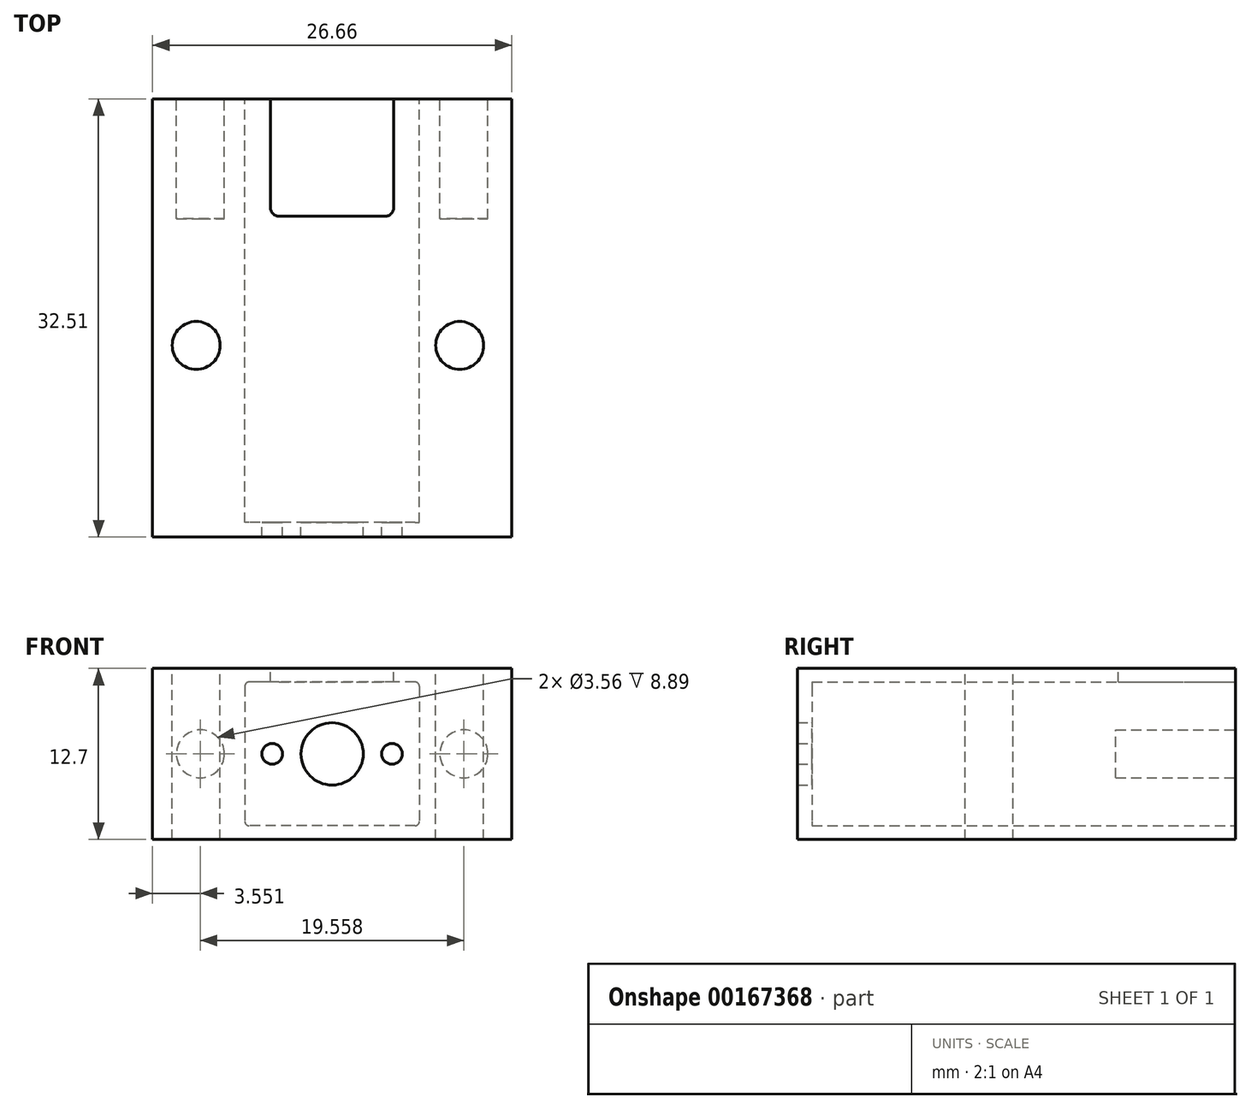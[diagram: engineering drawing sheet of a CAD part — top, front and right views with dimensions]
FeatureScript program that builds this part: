
annotation { "Feature Type Name" : "Feature", "Feature Type Description" : "" }
export const myFeature = defineFeature(function(context is Context, id is Id, definition is map)
    precondition{}
    {
        {
            var Q0;
            Q0=qCreatedBy(makeId("Front.planeOp"),FACE);
            var sketch = newSketch(context, id + "F0", { "sketchPlane" : qUnion([Q0])});
            skLineSegment(sketch, "E0.bottom", {"start": v(13.34, -6.35) * mm, "end": v(-13.33, -6.35) * mm});
            skLineSegment(sketch, "E0.top", {"start": v(13.33, 6.35) * mm, "end": v(-13.34, 6.35) * mm});
            skLineSegment(sketch, "E0.left", {"start": v(13.34, -6.35) * mm, "end": v(13.33, 6.35) * mm});
            skLineSegment(sketch, "E0.right", {"start": v(-13.33, -6.35) * mm, "end": v(-13.34, 6.35) * mm});
            skPoint(sketch, "E0.middle", {"position": v(0, 0) * mm});
            skCircle(sketch, "E1", {"center": v(0, 0) * mm, "radius": 2.31 * mm});
            skLineSegment(sketch, "E2.bottom", {"start": v(6.16, 5.33) * mm, "end": v(4.57, 5.33) * mm});
            skLineSegment(sketch, "E2.top", {"start": v(6.16, -5.33) * mm, "end": v(-6.16, -5.33) * mm});
            skLineSegment(sketch, "E2.left", {"start": v(6.48, 5.02) * mm, "end": v(6.48, -5.02) * mm});
            skLineSegment(sketch, "E2.right", {"start": v(-6.48, 5.02) * mm, "end": v(-6.48, -5.02) * mm});
            skLineSegment(sketch, "E3", {"start": v(-4.57, 5.33) * mm, "end": v(-4.57, 6.35) * mm});
            skLineSegment(sketch, "E4", {"start": v(4.57, 5.33) * mm, "end": v(4.57, 6.35) * mm});
            skLineSegment(sketch, "E5", {"start": v(4.57, 6.35) * mm, "end": v(-4.57, 6.35) * mm});
            skLineSegment(sketch, "E6.trimOffspring", {"start": v(-4.57, 5.33) * mm, "end": v(-6.16, 5.33) * mm});
            skLineSegment(sketch, "E7", {"start": v(-4.57, 5.33) * mm, "end": v(4.57, 5.33) * mm});
            skCircle(sketch, "E8", {"center": v(-9.78, 0) * mm, "radius": 1.78 * mm});
            skCircle(sketch, "E9", {"center": v(9.78, 0) * mm, "radius": 1.78 * mm});
            skPoint(sketch, "E10.visualSharp", {"position": v(-6.48, 5.33) * mm});
            skArc(sketch, "E10.filletArc", {"start": v(-6.16, 5.33) * mm, "mid": v(-6.38, 5.24) * mm, "end": v(-6.48, 5.02) * mm});
            skPoint(sketch, "E11.visualSharp", {"position": v(-6.48, -5.33) * mm});
            skArc(sketch, "E11.filletArc", {"start": v(-6.48, -5.02) * mm, "mid": v(-6.38, -5.24) * mm, "end": v(-6.16, -5.33) * mm});
            skPoint(sketch, "E12.visualSharp", {"position": v(6.48, -5.33) * mm});
            skArc(sketch, "E12.filletArc", {"start": v(6.16, -5.33) * mm, "mid": v(6.38, -5.24) * mm, "end": v(6.48, -5.02) * mm});
            skPoint(sketch, "E13.visualSharp", {"position": v(6.48, 5.33) * mm});
            skArc(sketch, "E13.filletArc", {"start": v(6.48, 5.02) * mm, "mid": v(6.38, 5.24) * mm, "end": v(6.16, 5.33) * mm});
            skCircle(sketch, "E14", {"center": v(-4.45, 0) * mm, "radius": 0.77 * mm});
            skCircle(sketch, "E15", {"center": v(4.45, 0) * mm, "radius": 0.77 * mm});
            skSolve(sketch);
        }
        {
            var Q0;
            Q0 = qSketchRegion(id + "F0", true);
            var Q1;
            Q1=makeQuery(id+"F0.imprint","IMPRINT",FACE,{"disambiguationData":[TD([[makeQuery(id+"F0.imprint","IMPRINT",EDGE,{"derivedFrom":sQuery(id+"F0.wireOp",EDGE,"E1")}),-1.0]])]});
            var Q2;
            Q2=makeQuery(id+"F0.imprint","IMPRINT",FACE,{"disambiguationData":[TD([[makeQuery(id+"F0.imprint","IMPRINT",EDGE,{"derivedFrom":sQuery(id+"F0.wireOp",EDGE,"E8")}),1.0]])]});
            var Q3;
            Q3=makeQuery(id+"F0.imprint","IMPRINT",FACE,{"disambiguationData":[TD([[makeQuery(id+"F0.imprint","IMPRINT",EDGE,{"derivedFrom":sQuery(id+"F0.wireOp",EDGE,"E9")}),1.0]])]});
            extrude(context, id + "F1", {"entities" : qUnion([Q0, Q1, Q2, Q3]), "depth" : 32.5 * mm});
        }
        {
            var Q0;
            Q0=makeQuery(id+"F0.imprint","IMPRINT",FACE,{"disambiguationData":[TD([[makeQuery(id+"F0.imprint","IMPRINT",EDGE,{"derivedFrom":sQuery(id+"F0.wireOp",EDGE,"E1")}),-1.0]])]});
            extrude(context, id + "F2", {"entities" : qUnion([Q0]), "operationType" : NewBodyOperationType.REMOVE, "depth" : 31.43 * mm});
        }
        {
            var Q0;
            Q0=makeQuery(id+"F0.imprint","IMPRINT",FACE,{"disambiguationData":[TD([[makeQuery(id+"F0.imprint","IMPRINT",EDGE,{"derivedFrom":sQuery(id+"F0.wireOp",EDGE,"E3")}),-1.0]])]});
            extrude(context, id + "F3", {"entities" : qUnion([Q0]), "operationType" : NewBodyOperationType.REMOVE, "depth" : 8.7 * mm});
        }
        {
            var Q0;
            Q0=makeQuery(id+"F0.imprint","IMPRINT",FACE,{"disambiguationData":[TD([[makeQuery(id+"F0.imprint","IMPRINT",EDGE,{"derivedFrom":sQuery(id+"F0.wireOp",EDGE,"E9")}),1.0]])]});
            var Q1;
            Q1=makeQuery(id+"F0.imprint","IMPRINT",FACE,{"disambiguationData":[TD([[makeQuery(id+"F0.imprint","IMPRINT",EDGE,{"derivedFrom":sQuery(id+"F0.wireOp",EDGE,"E8")}),1.0]])]});
            extrude(context, id + "F4", {"entities" : qUnion([Q0, Q1]), "operationType" : NewBodyOperationType.REMOVE, "depth" : 8.9 * mm});
        }
        {
            var Q0;
            Q0=makeQuery(id+"F1.opExtrude","SWEPT_FACE",FACE,{"disambiguationData":[OSD([sQuery(id+"F0.wireOp",EDGE,"E0.top"),sQuery(id+"F0.wireOp",EDGE,"E5")])]});
            var sketch = newSketch(context, id + "F5", { "sketchPlane" : qUnion([Q0])});
            skCircle(sketch, "E16", {"center": v(-10.09, -18.29) * mm, "radius": 1.78 * mm});
            skCircle(sketch, "E17", {"center": v(9.47, -18.29) * mm, "radius": 1.78 * mm});
            skSolve(sketch);
        }
        {
            var Q0;
            Q0 = qSketchRegion(id + "F5", true);
            extrude(context, id + "F6", {"entities" : qUnion([Q0]), "operationType" : NewBodyOperationType.REMOVE, "endBound" : BoundingType.THROUGH_ALL, "oppositeDirection" : true, "depth" : 25.4 * mm});
        }
        {
            var Q0;
            Q0=makeQuery(id+"F3.boolean.opBoolean","COPY",EDGE,{"derivedFrom":makeQuery(id+"F3.opExtrude","CAP_EDGE",EDGE,{"disambiguationData":[OSD([sQuery(id+"F0.wireOp",EDGE,"E3")])],"isStart":false})});
            var Q1;
            Q1=makeQuery(id+"F3.boolean.opBoolean","COPY",EDGE,{"derivedFrom":makeQuery(id+"F3.opExtrude","CAP_EDGE",EDGE,{"disambiguationData":[OSD([sQuery(id+"F0.wireOp",EDGE,"E4")])],"isStart":false})});
            var Q2;
            Q2=makeQuery(id+"F3.boolean.opBoolean","COPY",EDGE,{"derivedFrom":makeQuery(id+"F3.opExtrude","CAP_EDGE",EDGE,{"disambiguationData":[OSD([sQuery(id+"F0.wireOp",EDGE,"E4")])],"isStart":true})});
            var Q3;
            Q3=makeQuery(id+"F3.boolean.opBoolean","COPY",EDGE,{"derivedFrom":makeQuery(id+"F3.opExtrude","CAP_EDGE",EDGE,{"disambiguationData":[OSD([sQuery(id+"F0.wireOp",EDGE,"E3")])],"isStart":true})});
            fillet(context, id + "F7", {"entities" : qUnion([Q0, Q1, Q2, Q3]), "radius" : 0.64 * mm, "tangentPropagation" : true, "allowEdgeOverflow" : false});
        }
    });
